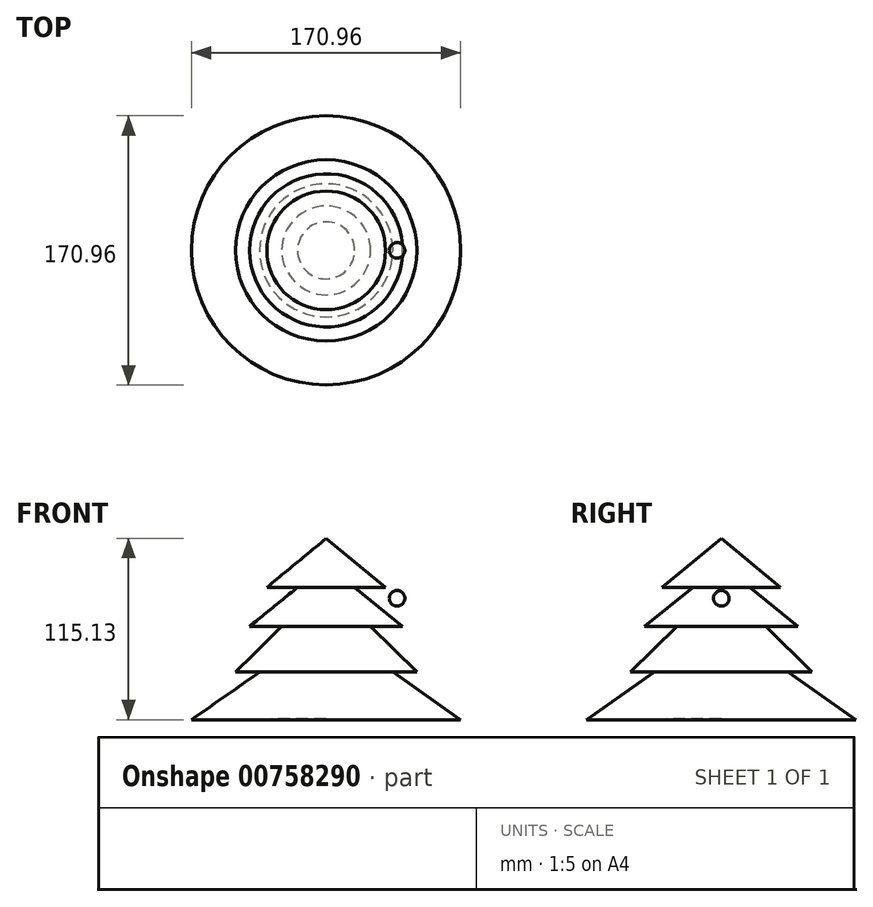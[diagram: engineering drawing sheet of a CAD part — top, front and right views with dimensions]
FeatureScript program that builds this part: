
annotation { "Feature Type Name" : "Feature", "Feature Type Description" : "" }
export const myFeature = defineFeature(function(context is Context, id is Id, definition is map)
    precondition{}
    {
        {
            var Q0;
            Q0=qCreatedBy(makeId("Front.planeOp"),FACE);
            var sketch = newSketch(context, id + "F0", { "sketchPlane" : qUnion([Q0])});
            skLineSegment(sketch, "E0", {"start": v(-45.04, -53.1) * mm, "end": v(-45.04, 61.45) * mm});
            skLineSegment(sketch, "E1", {"start": v(-45.04, 61.45) * mm, "end": v(-7.34, 30.36) * mm});
            skLineSegment(sketch, "E2", {"start": v(-7.34, 30.36) * mm, "end": v(-26.9, 30.36) * mm});
            skLineSegment(sketch, "E3", {"start": v(-26.9, 30.36) * mm, "end": v(3.6, 5.61) * mm});
            skLineSegment(sketch, "E4", {"start": v(3.6, 5.61) * mm, "end": v(-16.84, 5.61) * mm});
            skLineSegment(sketch, "E5", {"start": v(-16.84, 5.61) * mm, "end": v(12.52, -23.46) * mm});
            skLineSegment(sketch, "E6", {"start": v(12.52, -23.46) * mm, "end": v(-2.73, -23.46) * mm});
            skLineSegment(sketch, "E7", {"start": v(-2.73, -23.46) * mm, "end": v(40.44, -53.68) * mm});
            skLineSegment(sketch, "E8", {"start": v(40.44, -53.68) * mm, "end": v(-45.04, -53.1) * mm});
            skSolve(sketch);
        }
        {
            var Q0;
            Q0 = qSketchRegion(id + "F0", true);
            var Q1;
            Q1=sQuery(id+"F0.wireOp",EDGE,"E0");
            revolve(context, id + "F1", {"surfaceOperationType" : NewSurfaceOperationType.NEW, "entities" : qUnion([Q0]), "axis" : qUnion([Q1]), "revolveType" : RevolveType.FULL});
        }
        {
            var Q0;
            Q0=qCreatedBy(makeId("Right.planeOp"),FACE);
            var sketch = newSketch(context, id + "F2", { "sketchPlane" : qUnion([Q0])});
            skCircle(sketch, "E9", {"center": v(0, 23.46) * mm, "radius": 4.96 * mm});
            skLineSegment(sketch, "E10", {"start": v(0, 28.42) * mm, "end": v(0, 18.5) * mm});
            skSolve(sketch);
        }
        {
            var Q0;
            {var subQ0=sQuery(id+"F2.wireOp",EDGE,"E10");Q0=makeQuery(id+"F2.imprint","IMPRINT",FACE,{"disambiguationData":[TD([[makeQuery(id+"F2.imprint","IMPRINT",EDGE,{"derivedFrom":subQ0}),1.0]])]});}
            var Q1;
            Q1=sQuery(id+"F2.wireOp",EDGE,"E10");
            revolve(context, id + "F3", {"surfaceOperationType" : NewSurfaceOperationType.NEW, "entities" : qUnion([Q0]), "axis" : qUnion([Q1]), "revolveType" : RevolveType.FULL});
        }
    });
